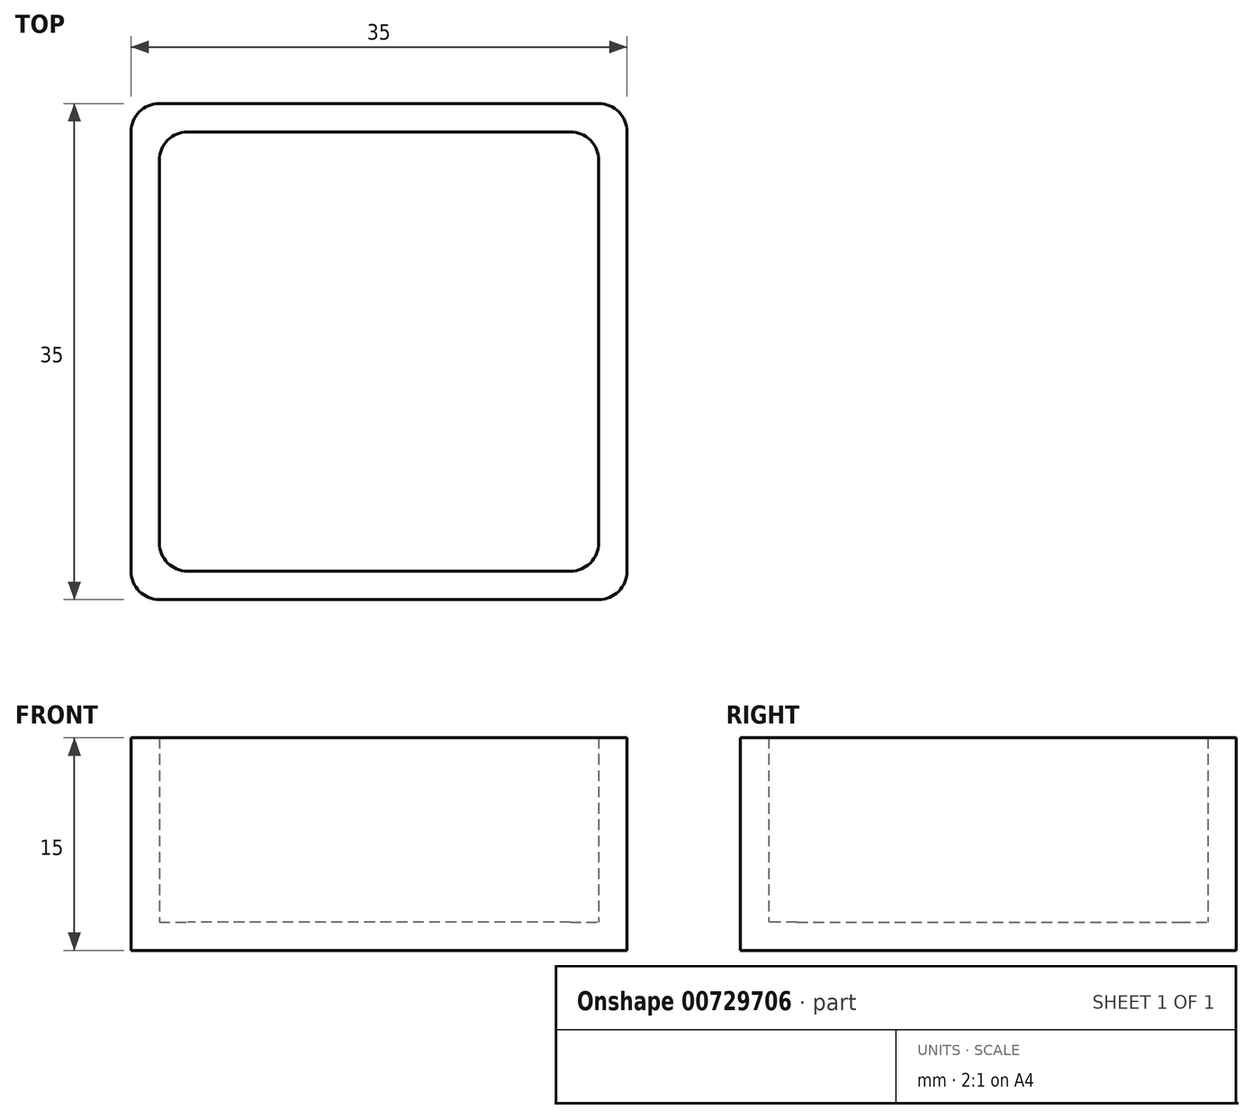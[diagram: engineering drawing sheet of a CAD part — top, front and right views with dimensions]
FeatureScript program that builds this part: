
annotation { "Feature Type Name" : "Feature", "Feature Type Description" : "" }
export const myFeature = defineFeature(function(context is Context, id is Id, definition is map)
    precondition{}
    {
        {
            var Q0;
            Q0=qCreatedBy(makeId("Top.planeOp"),FACE);
            var sketch = newSketch(context, id + "F0", { "sketchPlane" : qUnion([Q0])});
            skLineSegment(sketch, "E0.bottom", {"start": v(17.5, -17.5) * mm, "end": v(-17.5, -17.5) * mm});
            skLineSegment(sketch, "E0.top", {"start": v(17.5, 17.5) * mm, "end": v(-17.5, 17.5) * mm});
            skLineSegment(sketch, "E0.left", {"start": v(17.5, -17.5) * mm, "end": v(17.5, 17.5) * mm});
            skLineSegment(sketch, "E0.right", {"start": v(-17.5, -17.5) * mm, "end": v(-17.5, 17.5) * mm});
            skPoint(sketch, "E0.middle", {"position": v(0, 0) * mm});
            skSolve(sketch);
        }
        {
            var Q0;
            Q0=makeQuery(id+"F0.imprint","IMPRINT",FACE,{"disambiguationData":[TD([[makeQuery(id+"F0.imprint","IMPRINT",EDGE,{"derivedFrom":sQuery(id+"F0.wireOp",EDGE,"E0.bottom")}),-1.0]])]});
            extrude(context, id + "F1", {"entities" : qUnion([Q0]), "depth" : 15 * mm, "offsetDistance" : 25 * mm});
        }
        {
            var Q0;
            Q0=makeQuery(id+"F1.opExtrude","CAP_FACE",FACE,{"disambiguationData":[OSD([sQuery(id+"F0.wireOp",EDGE,"E0.bottom"),sQuery(id+"F0.wireOp",EDGE,"E0.top"),sQuery(id+"F0.wireOp",EDGE,"E0.left"),sQuery(id+"F0.wireOp",EDGE,"E0.right")])],"isStart":false});
            shell(context, id + "F2", {"entities" : qUnion([Q0]), "thickness" : 2 * mm});
        }
        {
            var Q0;
            Q0=makeQuery(id+"F1.opExtrude","SWEPT_EDGE",EDGE,{"disambiguationData":[OSD([sQuery(id+"F0.wireOp",EDGE,"E0.bottom"),sQuery(id+"F0.wireOp",EDGE,"E0.right")])]});
            var Q1;
            Q1=makeQuery(id+"F2.opShell","OFFSET_EDGE",EDGE,{"disambiguationData":[OSD([sQuery(id+"F0.wireOp",EDGE,"E0.top"),sQuery(id+"F0.wireOp",EDGE,"E0.left")])]});
            var Q2;
            Q2=makeQuery(id+"F1.opExtrude","SWEPT_EDGE",EDGE,{"disambiguationData":[OSD([sQuery(id+"F0.wireOp",EDGE,"E0.bottom"),sQuery(id+"F0.wireOp",EDGE,"E0.left")])]});
            var Q3;
            Q3=makeQuery(id+"F2.opShell","OFFSET_EDGE",EDGE,{"disambiguationData":[OSD([sQuery(id+"F0.wireOp",EDGE,"E0.top"),sQuery(id+"F0.wireOp",EDGE,"E0.right")])]});
            var Q4;
            Q4=makeQuery(id+"F1.opExtrude","SWEPT_EDGE",EDGE,{"disambiguationData":[OSD([sQuery(id+"F0.wireOp",EDGE,"E0.top"),sQuery(id+"F0.wireOp",EDGE,"E0.left")])]});
            var Q5;
            Q5=makeQuery(id+"F1.opExtrude","SWEPT_EDGE",EDGE,{"disambiguationData":[OSD([sQuery(id+"F0.wireOp",EDGE,"E0.top"),sQuery(id+"F0.wireOp",EDGE,"E0.right")])]});
            var Q6;
            Q6=makeQuery(id+"F2.opShell","OFFSET_EDGE",EDGE,{"disambiguationData":[OSD([sQuery(id+"F0.wireOp",EDGE,"E0.bottom"),sQuery(id+"F0.wireOp",EDGE,"E0.left")])]});
            var Q7;
            Q7=makeQuery(id+"F2.opShell","OFFSET_EDGE",EDGE,{"disambiguationData":[OSD([sQuery(id+"F0.wireOp",EDGE,"E0.bottom"),sQuery(id+"F0.wireOp",EDGE,"E0.right")])]});
            fillet(context, id + "F3", {"entities" : qUnion([Q0, Q1, Q2, Q3, Q4, Q5, Q6, Q7]), "radius" : 2 * mm, "tangentPropagation" : true, "allowEdgeOverflow" : false});
        }
    });
